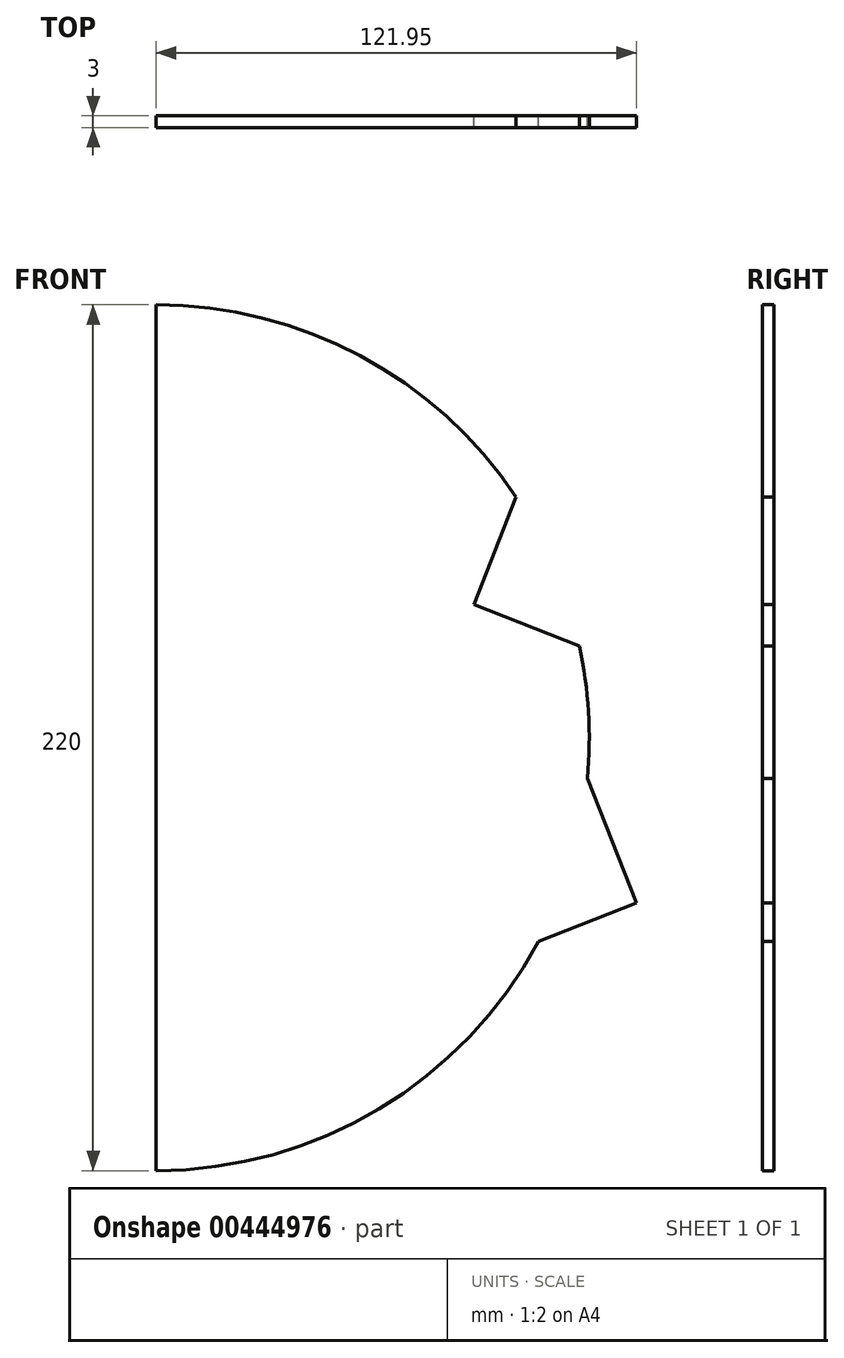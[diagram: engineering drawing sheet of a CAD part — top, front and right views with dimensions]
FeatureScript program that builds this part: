
annotation { "Feature Type Name" : "Feature", "Feature Type Description" : "" }
export const myFeature = defineFeature(function(context is Context, id is Id, definition is map)
    precondition{}
    {
        {
            var Q0;
            Q0=qCreatedBy(makeId("Front.planeOp"),FACE);
            var sketch = newSketch(context, id + "F0", { "sketchPlane" : qUnion([Q0])});
            skArc(sketch, "E0", {"start": v(0, -110) * mm, "mid": v(56.6, -94.32) * mm, "end": v(97.06, -51.76) * mm});
            skLineSegment(sketch, "E1", {"start": v(0, 110) * mm, "end": v(0, -110) * mm});
            skLineSegment(sketch, "E2", {"start": v(91.41, 61.19) * mm, "end": v(80.7, 33.87) * mm});
            skLineSegment(sketch, "E3", {"start": v(80.7, 33.87) * mm, "end": v(107.5, 23.36) * mm});
            skArc(sketch, "E4.trimOffspring", {"start": v(91.41, 61.19) * mm, "mid": v(51.81, 97.03) * mm, "end": v(0, 110) * mm});
            skLineSegment(sketch, "E5", {"start": v(109.52, -10.3) * mm, "end": v(121.95, -41.99) * mm});
            skLineSegment(sketch, "E6", {"start": v(121.95, -41.99) * mm, "end": v(97.06, -51.76) * mm});
            skArc(sketch, "E7.trimOffspring", {"start": v(109.52, -10.3) * mm, "mid": v(109.8, 6.6) * mm, "end": v(107.5, 23.36) * mm});
            skSolve(sketch);
        }
        {
            var Q0;
            Q0 = qSketchRegion(id + "F0", true);
            extrude(context, id + "F1", {"entities" : qUnion([Q0]), "depth" : 3 * mm});
        }
    });
